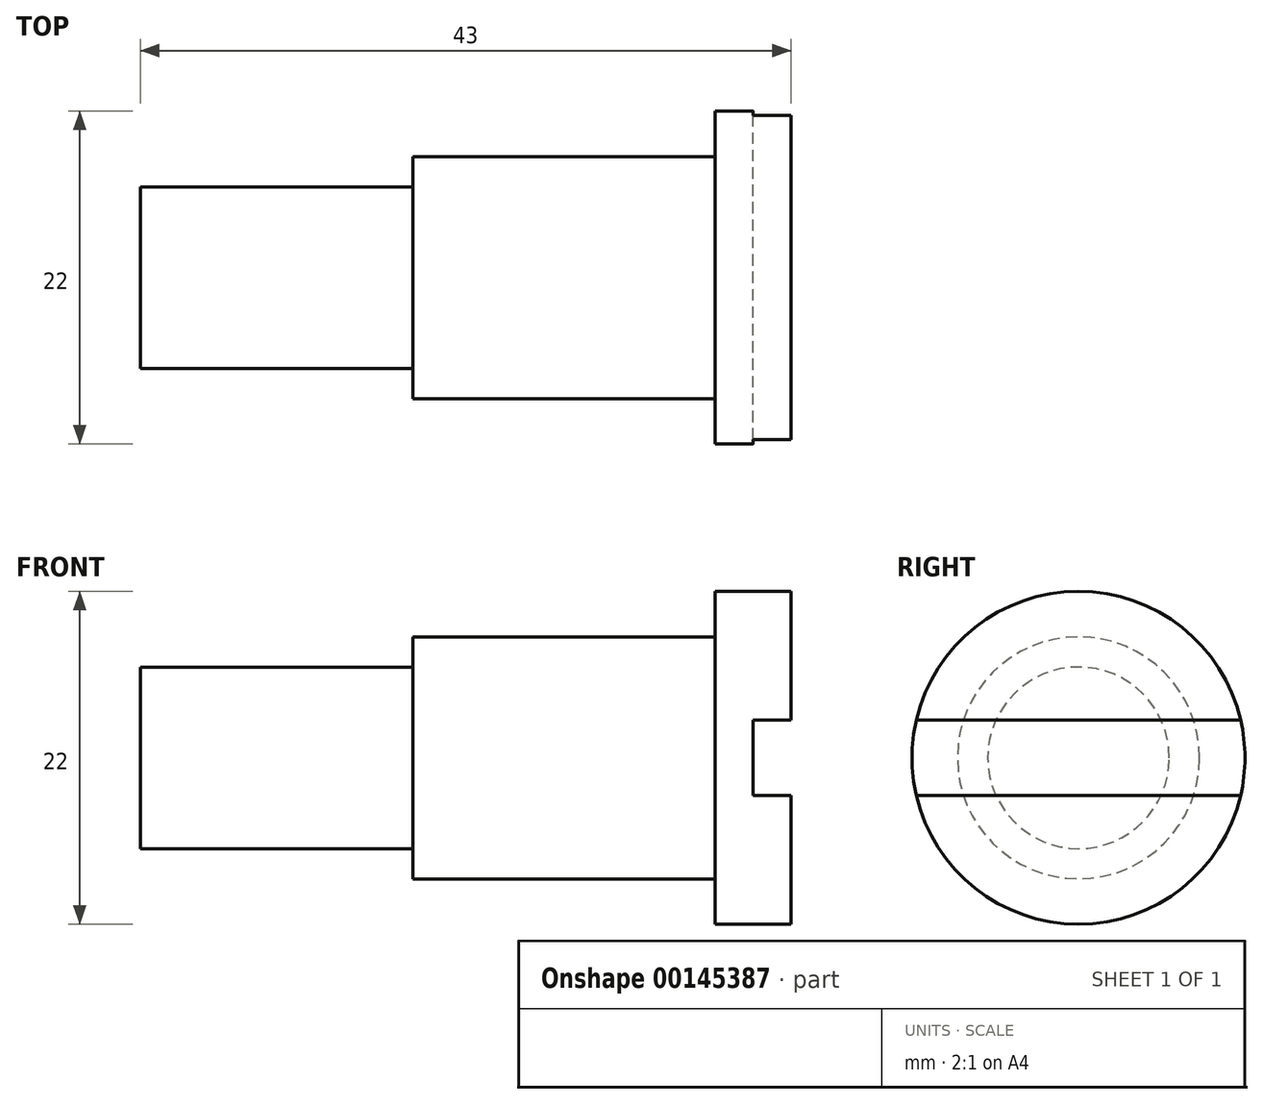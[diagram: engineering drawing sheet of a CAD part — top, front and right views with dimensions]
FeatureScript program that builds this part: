
annotation { "Feature Type Name" : "Feature", "Feature Type Description" : "" }
export const myFeature = defineFeature(function(context is Context, id is Id, definition is map)
    precondition{}
    {
        {
            var Q0;
            Q0=qCreatedBy(makeId("Front.planeOp"),FACE);
            var sketch = newSketch(context, id + "F0", { "sketchPlane" : qUnion([Q0])});
            skLineSegment(sketch, "E0", {"start": v(-62.56, 0) * mm, "end": v(41.68, 0) * mm, "construction": true});
            skLineSegment(sketch, "E1", {"start": v(-38, 0) * mm, "end": v(-38, 6) * mm});
            skLineSegment(sketch, "E2", {"start": v(-38, 6) * mm, "end": v(-20, 6) * mm});
            skLineSegment(sketch, "E3", {"start": v(-20, 6) * mm, "end": v(-20, 8) * mm});
            skLineSegment(sketch, "E4", {"start": v(-20, 8) * mm, "end": v(0, 8) * mm});
            skLineSegment(sketch, "E5", {"start": v(0, 8) * mm, "end": v(0, 11) * mm});
            skLineSegment(sketch, "E6", {"start": v(0, 11) * mm, "end": v(5, 11) * mm});
            skLineSegment(sketch, "E7", {"start": v(5, 11) * mm, "end": v(5, 0) * mm});
            skLineSegment(sketch, "E8", {"start": v(-38, 0) * mm, "end": v(5, 0) * mm});
            skSolve(sketch);
        }
        {
            var Q0;
            Q0=qSketchRegion(id+"F0",true);
            var Q1;
            Q1=sQuery(id+"F0.wireOp",EDGE,"E0");
            revolve(context, id + "F1", {"entities" : qUnion([Q0]), "axis" : qUnion([Q1]), "revolveType" : RevolveType.FULL});
        }
        {
            var Q0;
            Q0=makeQuery(id+"F1.opRevolve","SWEPT_FACE",FACE,{"disambiguationData":[OSD([sQuery(id+"F0.wireOp",EDGE,"E7")])]});
            var sketch = newSketch(context, id + "F2", { "sketchPlane" : qUnion([Q0])});
            skLineSegment(sketch, "E9.bottom", {"start": v(-33.15, 2.5) * mm, "end": v(29.04, 2.5) * mm});
            skLineSegment(sketch, "E9.top", {"start": v(-33.15, -2.5) * mm, "end": v(29.04, -2.5) * mm});
            skLineSegment(sketch, "E9.left", {"start": v(-33.15, 2.5) * mm, "end": v(-33.15, -2.5) * mm});
            skLineSegment(sketch, "E9.right", {"start": v(29.04, 2.5) * mm, "end": v(29.04, -2.5) * mm});
            skSolve(sketch);
        }
        {
            var Q0;
            Q0=qSketchRegion(id+"F2",true);
            extrude(context, id + "F3", {"entities" : qUnion([Q0]), "operationType" : NewBodyOperationType.REMOVE, "oppositeDirection" : true, "depth" : 2.5 * mm});
        }
    });
